# Revit family: Haworth_Openest_Accessories_Pillows
name_source: partatom
category: Furniture
revit_build: Autodesk Revit 2018 (Build: 20170223_1515(x64)
units: mm (PartAtom-declared; Revit-internal decimal feet)

## family parameters
Always vertical = Yes
Cut with Voids When Loaded = No
OmniClass Number = 23.40.20.00
OmniClass Title = General Furniture and Specialties
Room Calculation Point = No
Shared = No
Work Plane-Based = No

## types (2) — shared parameters
Assembly Code = E2020200
Description = Haworth - Openest - Accessories - Pillows
Manufacturer = Haworth
Model = HOUP
Size = Verify Final Dim. w/ Haworth
Sustainability Info = https://www.haworth.com
URL = http://www.haworth.com
URL - Product = https://www.haworth.com
Version = 2
Warranty = http://www.haworth.com

## per-type parameters (varying)
| type | Height | HeightCore | Rectangular | Square | Width | WidthCore |
| Pillow - Square | 1' - 6" | 0' - 6 15/16" | No | Yes | 1' - 6" | 0' - 6 15/16" |
| Pillow - Rectangle | 1' - 4" | 0' - 4 15/16" | Yes | No | 2' - 0" | 1' - 0 15/16" |

## geometry (parser evidence)
native form markers: Sweep x5
no freeform markers — native parametric forms only
